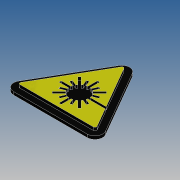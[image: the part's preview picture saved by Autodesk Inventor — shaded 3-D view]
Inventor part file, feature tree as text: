
AUTODESK INVENTOR PART (.ipt)
format: ipt  version: 2019 (Build 230136000, 136)  size: 312,832 bytes
history: native  units: mm
features: extrude x5, sketch x5, pattern_circular x2, fillet x1, projected_geometry x1
ambient origin geometry x8: Origin, YZ Plane, XZ Plane, XY Plane, X Axis, Y Axis, Z Axis, Center Point
bodies: Solid1 (feature_tree)
feature tree (14):
  extrude  "Extrusion1"  Depth=0.4mm TaperAngle=0.0deg
  fillet  "Fillet1"  Radius=1.0mm
  extrude  "Extrusion2"  Depth=0.8mm
  extrude  "Extrusion3"  Depth=0.3mm
  pattern_circular  "Circular Pattern1"  Count=8 Angle=360.0deg
  extrude  "Extrusion4"  TaperAngle=22.5deg  [1 undecoded]
  pattern_circular  "Circular Pattern2"  [2 undecoded]
  extrude  "Extrusion5"  Depth=0.4mm
  sketch  "Sketch1"  dims[d0=13.0mm d1=0.4mm d2=0.0mm d3=1.0mm]
  sketch  "Sketch2"  dims[d4=0.8mm d5=2.5mm]
  sketch  "Sketch3"  dims[d6=0.4mm d7=0.0mm d8=0.3mm]
  sketch  "Sketch4"  dims[d9=2.5mm]
  sketch  "Sketch5"  dims[d10=0.4mm d11=0.0mm d12=80.0mm d13=360.0deg d15=22.5deg d16=0.3mm d17=2.0mm d18=0.4mm d19=0.0mm d20=80.0mm d21=360.0deg d23=0.4mm d24=0.0mm]
  projected_geometry  "Project Cut Edges1"
note: 3 required parameter values undecoded (feature->parameter linkage not recoverable at this tier; creation-order binding heuristic only, values carry confidence <= 0.55)
